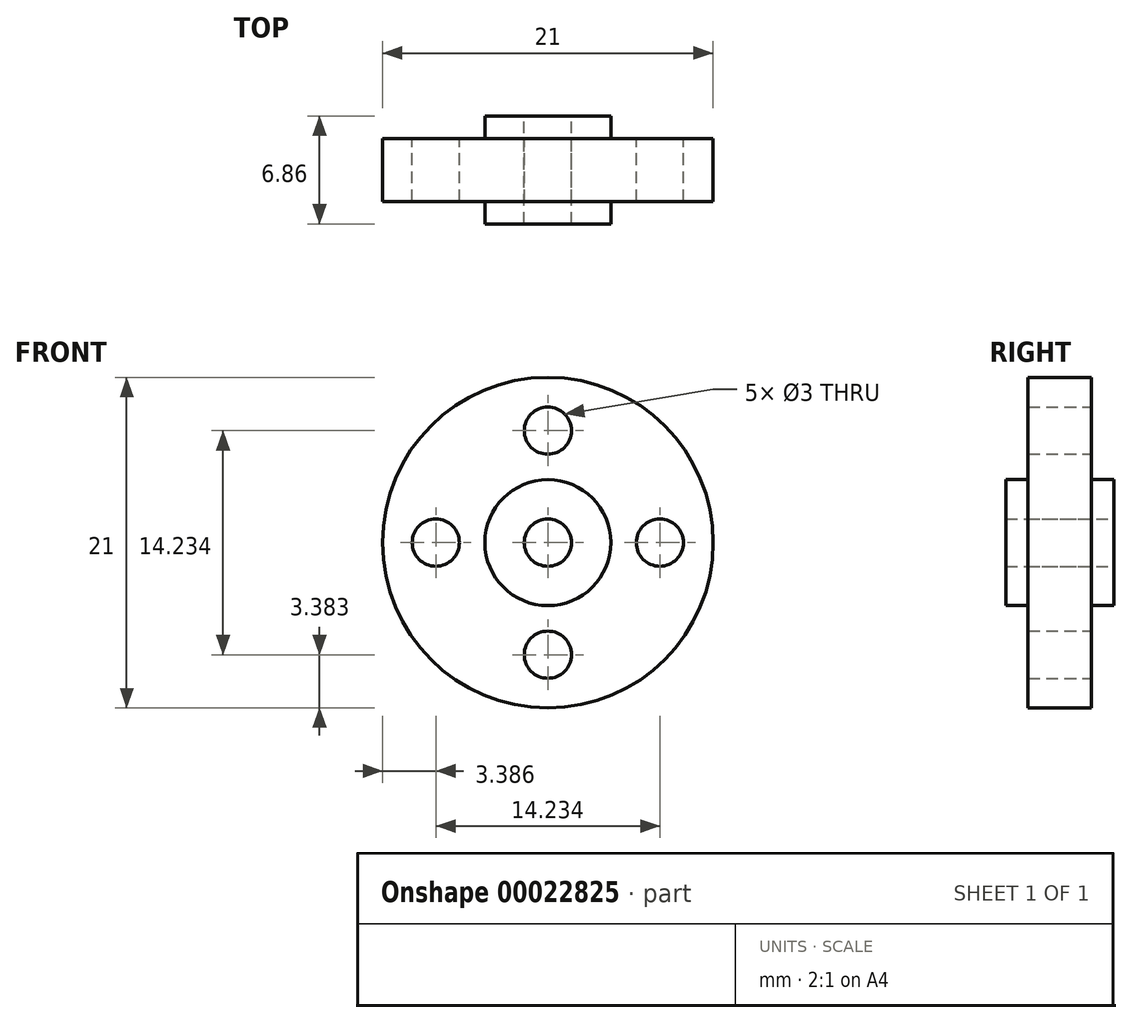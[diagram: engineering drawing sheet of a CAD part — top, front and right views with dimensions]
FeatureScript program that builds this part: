
annotation { "Feature Type Name" : "Feature", "Feature Type Description" : "" }
export const myFeature = defineFeature(function(context is Context, id is Id, definition is map)
    precondition{}
    {
        {
            var Q0;
            Q0=qCreatedBy(makeId("Front.planeOp"),FACE);
            var sketch = newSketch(context, id + "F0", { "sketchPlane" : qUnion([Q0])});
            skCircle(sketch, "E0", {"center": v(-34.42, 0) * mm, "radius": 10.5 * mm});
            skCircle(sketch, "E1", {"center": v(-34.42, 0) * mm, "radius": 4 * mm});
            skCircle(sketch, "E2", {"center": v(-34.42, 0) * mm, "radius": 1.5 * mm});
            skLineSegment(sketch, "E3", {"start": v(-34.42, 4) * mm, "end": v(-34.42, 5.62) * mm});
            skCircle(sketch, "E4", {"center": v(-34.42, 7.12) * mm, "radius": 1.5 * mm});
            skCircle(sketch, "E5.1.0", {"center": v(-41.53, 0) * mm, "radius": 1.5 * mm});
            skCircle(sketch, "E5.2.0", {"center": v(-34.42, -7.12) * mm, "radius": 1.5 * mm});
            skCircle(sketch, "E5.3.0", {"center": v(-27.3, 0) * mm, "radius": 1.5 * mm});
            skSolve(sketch);
        }
        {
            var Q0;
            Q0=makeQuery(id+"F0.imprint","IMPRINT",FACE,{"disambiguationData":[TD([[makeQuery(id+"F0.imprint","IMPRINT",EDGE,{"derivedFrom":sQuery(id+"F0.wireOp",EDGE,"E0")}),1.0]])]});
            extrude(context, id + "F1", {"entities" : qUnion([Q0]), "endBound" : BoundingType.SYMMETRIC, "depth" : 4 * mm});
        }
        {
            var Q0;
            Q0=makeQuery(id+"F0.imprint","IMPRINT",FACE,{"disambiguationData":[TD([[makeQuery(id+"F0.imprint","IMPRINT",EDGE,{"derivedFrom":sQuery(id+"F0.wireOp",EDGE,"E1")}),1.0]])]});
            var Q1;
            Q1=sQuery(id+"F0.wireOp",EDGE,"E1");
            extrude(context, id + "F2", {"entities" : qUnion([Q0]), "operationType" : NewBodyOperationType.ADD, "surfaceEntities" : qUnion([Q1]), "endBound" : BoundingType.SYMMETRIC, "depth" : 6.86 * mm});
        }
    });
